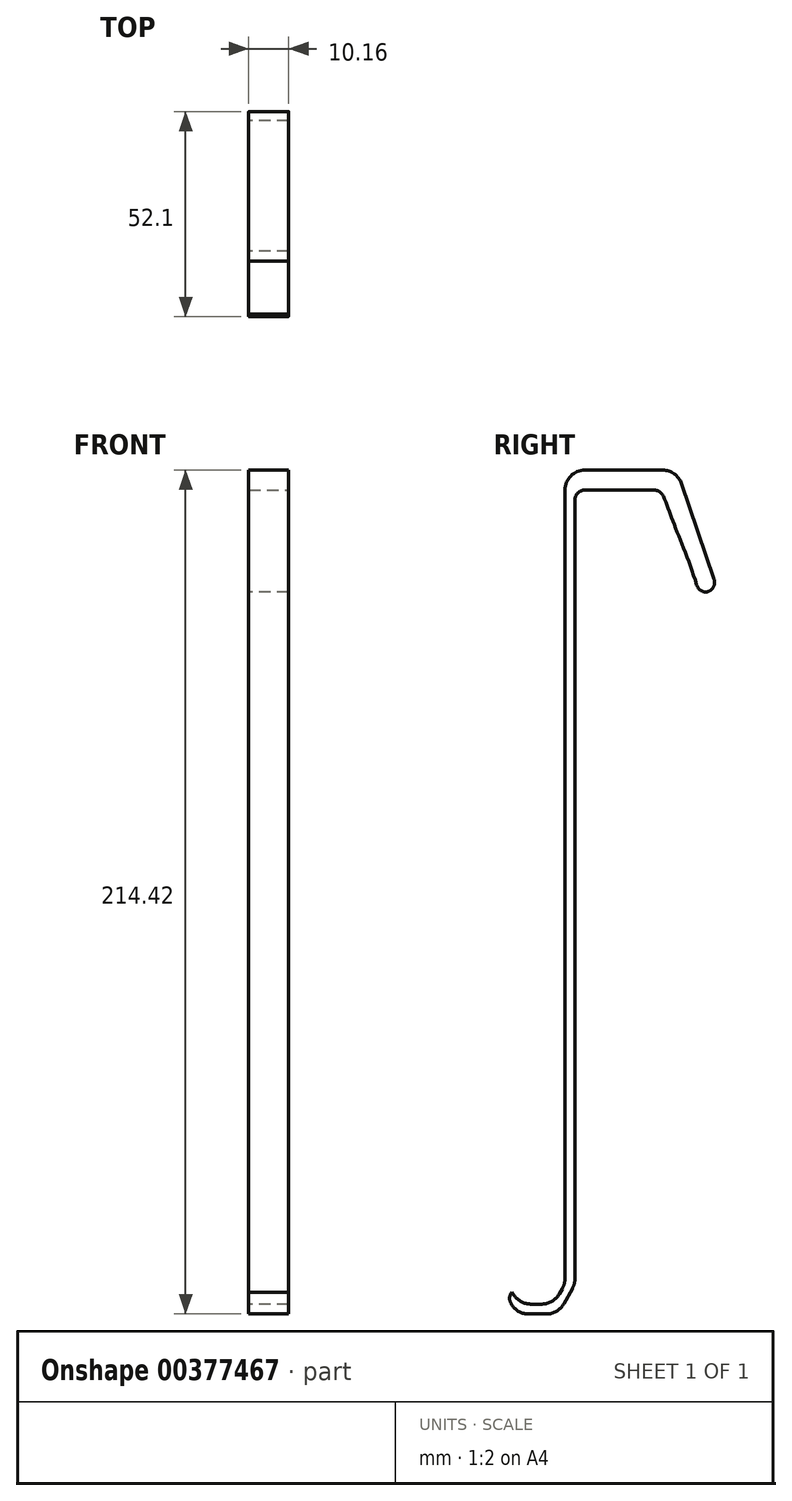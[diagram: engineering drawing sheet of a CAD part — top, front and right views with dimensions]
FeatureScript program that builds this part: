
annotation { "Feature Type Name" : "Feature", "Feature Type Description" : "" }
export const myFeature = defineFeature(function(context is Context, id is Id, definition is map)
    precondition{}
    {
        {
            var Q0;
            Q0=qCreatedBy(makeId("Right.planeOp"),FACE);
            var sketch = newSketch(context, id + "F0", { "sketchPlane" : qUnion([Q0])});
            skLineSegment(sketch, "E0", {"start": v(0, 0) * mm, "end": v(17.27, 0) * mm});
            skFitSpline(sketch, "E1", {"points": [v(17.27, 0) * mm, v(32.21, -47.7) * mm, v(37.99, -84.26) * mm], "startDerivative": vector(32.39, -88.5) * mm, "endDerivative": vector(-0.32, -77.24) * mm});
            skLineSegment(sketch, "E2", {"start": v(0, 0) * mm, "end": v(0, -304.8) * mm});
            skLineSegment(sketch, "E3.bottom", {"start": v(-15.33, -19.05) * mm, "end": v(-6.7, -19.05) * mm});
            skLineSegment(sketch, "E3.top", {"start": v(-15.33, -204.47) * mm, "end": v(-6.7, -204.47) * mm});
            skLineSegment(sketch, "E3.left", {"start": v(-15.33, -19.05) * mm, "end": v(-15.33, -204.47) * mm});
            skLineSegment(sketch, "E3.right", {"start": v(-6.7, -19.05) * mm, "end": v(-6.7, -204.47) * mm});
            skLineSegment(sketch, "E4", {"start": v(-3.17, -200.45) * mm, "end": v(-3.18, 1.27) * mm});
            skLineSegment(sketch, "E5", {"start": v(-3.18, 1.27) * mm, "end": v(18.56, 1.27) * mm});
            skFitSpline(sketch, "E6", {"points": [v(18.56, 1.27) * mm, v(22.14, -7.68) * mm, v(28.27, -24.66) * mm], "startDerivative": vector(10.18, -20.64) * mm, "endDerivative": vector(8.72, -33.4) * mm});
            skLineSegment(sketch, "E7", {"start": v(28.27, -24.66) * mm, "end": v(33.35, -24.66) * mm});
            skLineSegment(sketch, "E8", {"start": v(33.35, -24.66) * mm, "end": v(22.75, 6.35) * mm});
            skLineSegment(sketch, "E9", {"start": v(22.75, 6.35) * mm, "end": v(-5.72, 6.35) * mm});
            skLineSegment(sketch, "E10", {"start": v(-5.72, 6.35) * mm, "end": v(-5.71, -200.45) * mm});
            skLineSegment(sketch, "E11", {"start": v(-5.71, -200.45) * mm, "end": v(-3.17, -200.45) * mm, "construction": true});
            skLineSegment(sketch, "E12", {"start": v(-3.17, -200.45) * mm, "end": v(-7.46, -208.07) * mm});
            skLineSegment(sketch, "E13", {"start": v(-7.46, -208.07) * mm, "end": v(-17.62, -208.07) * mm});
            skLineSegment(sketch, "E14", {"start": v(-17.62, -208.07) * mm, "end": v(-21.4, -202.51) * mm});
            skLineSegment(sketch, "E15", {"start": v(-21.4, -202.51) * mm, "end": v(-19.16, -202.51) * mm});
            skLineSegment(sketch, "E16", {"start": v(-19.16, -202.51) * mm, "end": v(-17.09, -205.55) * mm});
            skLineSegment(sketch, "E17", {"start": v(-17.09, -205.55) * mm, "end": v(-8.59, -205.55) * mm});
            skLineSegment(sketch, "E18", {"start": v(-8.59, -205.55) * mm, "end": v(-5.71, -200.45) * mm});
            skSolve(sketch);
        }
        {
            var Q0;
            Q0=makeQuery(id+"F0.imprint","IMPRINT",FACE,{"disambiguationData":[TD([[makeQuery(id+"F0.imprint","IMPRINT",EDGE,{"derivedFrom":sQuery(id+"F0.wireOp",EDGE,"E4")}),1.0]])]});
            var Q1;
            {var subQ0=sQuery(id+"F0.wireOp",EDGE,"E3.right");var subQ1=sQuery(id+"F0.wireOp",EDGE,"E3.top");var subQ2=makeQuery(id+"F0.imprint","INTERSECT",VERTEX,{"derivedFrom":[subQ1,subQ0]});Q1=makeQuery(id+"F0.imprint","IMPRINT",FACE,{"disambiguationData":[TD([[makeQuery(id+"F0.imprint","IMPRINT",EDGE,{"disambiguationData":[TD([[subQ2,1.0]])],"derivedFrom":subQ1}),1.0]])]});}
            extrude(context, id + "F1", {"entities" : qUnion([Q0, Q1]), "depth" : 10.16 * mm});
        }
        {
            var Q0;
            Q0=makeQuery(id+"F1.opExtrude","SWEPT_EDGE",EDGE,{"disambiguationData":[OSD([sQuery(id+"F0.wireOp",EDGE,"E16"),sQuery(id+"F0.wireOp",EDGE,"E17")])]});
            var Q1;
            Q1=makeQuery(id+"F1.opExtrude","SWEPT_EDGE",EDGE,{"disambiguationData":[OSD([sQuery(id+"F0.wireOp",EDGE,"E17"),sQuery(id+"F0.wireOp",EDGE,"E18")])]});
            var Q2;
            Q2=makeQuery(id+"F1.opExtrude","SWEPT_EDGE",EDGE,{"disambiguationData":[OSD([sQuery(id+"F0.wireOp",EDGE,"E10"),sQuery(id+"F0.wireOp",EDGE,"E18")])]});
            var Q3;
            Q3=makeQuery(id+"F1.opExtrude","SWEPT_EDGE",EDGE,{"disambiguationData":[OSD([sQuery(id+"F0.wireOp",EDGE,"E4"),sQuery(id+"F0.wireOp",EDGE,"E12")])]});
            var Q4;
            Q4=makeQuery(id+"F1.opExtrude","SWEPT_EDGE",EDGE,{"disambiguationData":[OSD([sQuery(id+"F0.wireOp",EDGE,"E12"),sQuery(id+"F0.wireOp",EDGE,"E13")])]});
            var Q5;
            Q5=makeQuery(id+"F1.opExtrude","SWEPT_EDGE",EDGE,{"disambiguationData":[OSD([sQuery(id+"F0.wireOp",EDGE,"E13"),sQuery(id+"F0.wireOp",EDGE,"E14")])]});
            var Q6;
            Q6=makeQuery(id+"F1.opExtrude","SWEPT_EDGE",EDGE,{"disambiguationData":[OSD([sQuery(id+"F0.wireOp",EDGE,"E8"),sQuery(id+"F0.wireOp",EDGE,"E9")])]});
            var Q7;
            Q7=makeQuery(id+"F1.opExtrude","SWEPT_EDGE",EDGE,{"disambiguationData":[OSD([sQuery(id+"F0.wireOp",EDGE,"E9"),sQuery(id+"F0.wireOp",EDGE,"E10")])]});
            fillet(context, id + "F2", {"entities" : qUnion([Q0, Q1, Q2, Q3, Q4, Q5, Q6, Q7]), "radius" : 5.08 * mm, "tangentPropagation" : true, "allowEdgeOverflow" : false});
        }
        {
            var Q0;
            Q0=makeQuery(id+"F1.opExtrude","SWEPT_EDGE",EDGE,{"disambiguationData":[OSD([sQuery(id+"F0.wireOp",EDGE,"E14"),sQuery(id+"F0.wireOp",EDGE,"E15")])]});
            var Q1;
            Q1=makeQuery(id+"F1.opExtrude","SWEPT_EDGE",EDGE,{"disambiguationData":[OSD([sQuery(id+"F0.wireOp",EDGE,"E4"),sQuery(id+"F0.wireOp",EDGE,"E5")])]});
            var Q2;
            Q2=makeQuery(id+"F1.opExtrude","SWEPT_EDGE",EDGE,{"disambiguationData":[OSD([sQuery(id+"F0.wireOp",EDGE,"E5"),sQuery(id+"F0.wireOp",EDGE,"E6")])]});
            var Q3;
            Q3=makeQuery(id+"F1.opExtrude","SWEPT_EDGE",EDGE,{"disambiguationData":[OSD([sQuery(id+"F0.wireOp",EDGE,"E7"),sQuery(id+"F0.wireOp",EDGE,"E8")])]});
            var Q4;
            Q4=makeQuery(id+"F1.opExtrude","SWEPT_EDGE",EDGE,{"disambiguationData":[OSD([sQuery(id+"F0.wireOp",EDGE,"E6"),sQuery(id+"F0.wireOp",EDGE,"E7")])]});
            fillet(context, id + "F3", {"entities" : qUnion([Q0, Q1, Q2, Q3, Q4]), "radius" : 2.54 * mm, "tangentPropagation" : true, "allowEdgeOverflow" : false});
        }
    });
